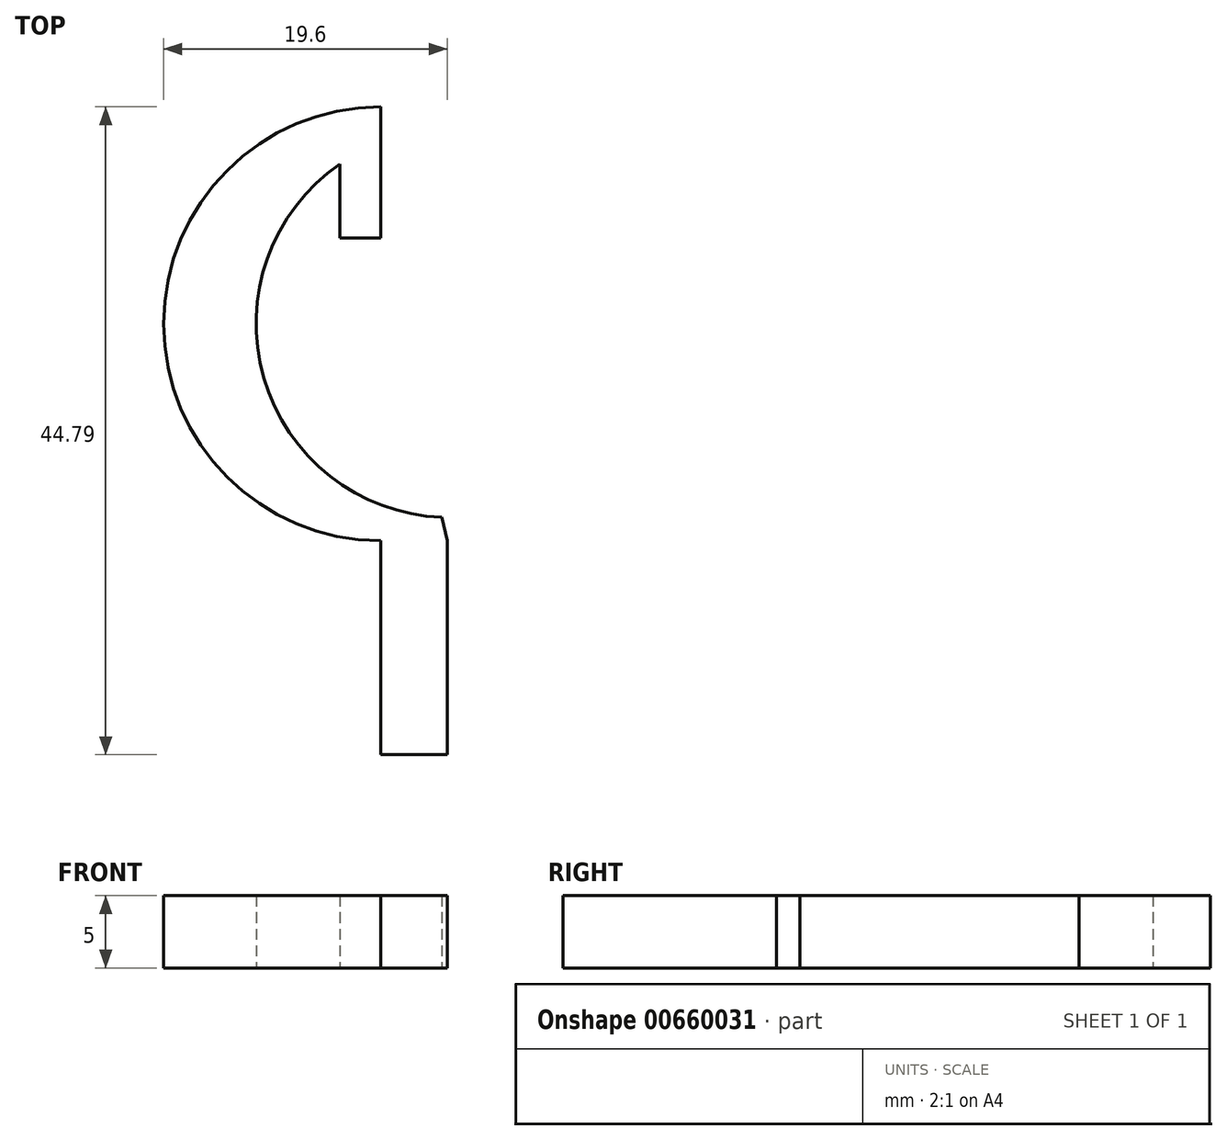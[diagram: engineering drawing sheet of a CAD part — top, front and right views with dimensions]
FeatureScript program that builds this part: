
annotation { "Feature Type Name" : "Feature", "Feature Type Description" : "" }
export const myFeature = defineFeature(function(context is Context, id is Id, definition is map)
    precondition{}
    {
        {
            var Q0;
            Q0=qCreatedBy(makeId("Top.planeOp"),FACE);
            var sketch = newSketch(context, id + "F0", { "sketchPlane" : qUnion([Q0])});
            skArc(sketch, "E0", {"start": v(0, 15) * mm, "mid": v(-15, 0) * mm, "end": v(0, -15) * mm});
            skLineSegment(sketch, "E1", {"start": v(0, 15) * mm, "end": v(0, 5.92) * mm});
            skLineSegment(sketch, "E2", {"start": v(-2.8, 14.74) * mm, "end": v(-2.8, 5.92) * mm});
            skLineSegment(sketch, "E3", {"start": v(-2.8, 5.92) * mm, "end": v(0, 5.92) * mm});
            skLineSegment(sketch, "E4", {"start": v(0, -15) * mm, "end": v(0, -29.79) * mm});
            skLineSegment(sketch, "E5", {"start": v(0, -29.79) * mm, "end": v(4.6, -29.79) * mm});
            skLineSegment(sketch, "E6", {"start": v(4.6, -29.79) * mm, "end": v(4.6, -15) * mm});
            skArc(sketch, "E7", {"start": v(-2.8, 11.04) * mm, "mid": v(-8.08, -3.71) * mm, "end": v(4.24, -13.39) * mm});
            skLineSegment(sketch, "E8", {"start": v(4.24, -13.39) * mm, "end": v(4.6, -15) * mm});
            skSolve(sketch);
        }
        {
            var Q0;
            {var subQ4=sQuery(id+"F0.wireOp",EDGE,"E4");Q0=makeQuery(id+"F0.imprint","IMPRINT",FACE,{"disambiguationData":[TD([[makeQuery(id+"F0.imprint","IMPRINT",EDGE,{"derivedFrom":subQ4}),1.0]])]});}
            var Q1;
            {var subQ5=sQuery(id+"F0.wireOp",EDGE,"E1");Q1=makeQuery(id+"F0.imprint","IMPRINT",FACE,{"disambiguationData":[TD([[makeQuery(id+"F0.imprint","IMPRINT",EDGE,{"derivedFrom":subQ5}),-1.0]])]});}
            extrude(context, id + "F1", {"entities" : qUnion([Q0, Q1]), "depth" : 5 * mm, "offsetDistance" : 25 * mm});
        }
    });
